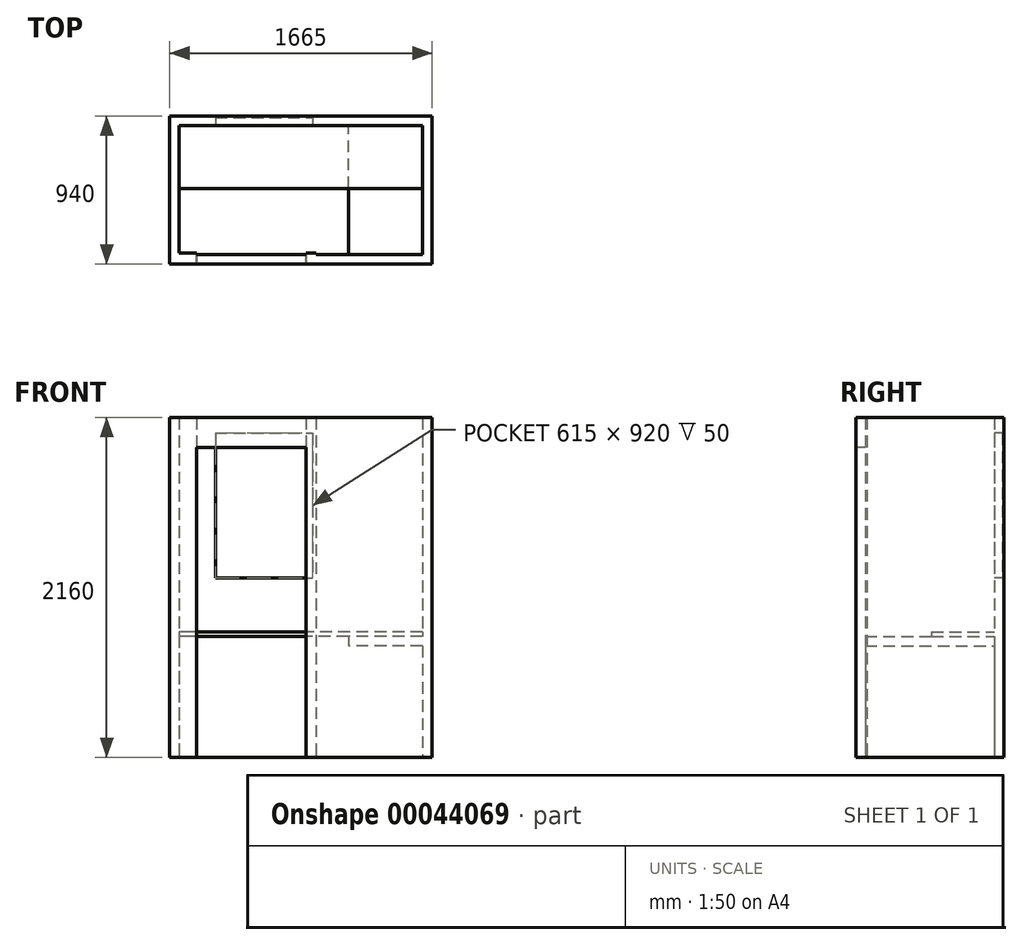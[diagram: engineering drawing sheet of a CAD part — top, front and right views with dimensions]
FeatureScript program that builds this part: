
annotation { "Feature Type Name" : "Feature", "Feature Type Description" : "" }
export const myFeature = defineFeature(function(context is Context, id is Id, definition is map)
    precondition{}
    {
        {
            var Q0;
            Q0=qCreatedBy(makeId("Top.planeOp"),FACE);
            var sketch = newSketch(context, id + "F0", { "sketchPlane" : qUnion([Q0])});
            skLineSegment(sketch, "E0.bottom", {"start": v(-570.89, 899.88) * mm, "end": v(974.11, 899.88) * mm});
            skLineSegment(sketch, "E0.top", {"start": v(234.11, 79.88) * mm, "end": v(974.11, 79.88) * mm});
            skLineSegment(sketch, "E0.left", {"start": v(-570.89, 899.88) * mm, "end": v(-570.89, 79.88) * mm});
            skLineSegment(sketch, "E0.right", {"start": v(974.11, 899.88) * mm, "end": v(974.11, 79.88) * mm});
            skLineSegment(sketch, "E1.0", {"start": v(-630.89, 959.88) * mm, "end": v(1034.11, 959.88) * mm});
            skLineSegment(sketch, "E1.1", {"start": v(-630.89, 959.88) * mm, "end": v(-630.89, 19.88) * mm});
            skLineSegment(sketch, "E1.2", {"start": v(-630.89, 19.88) * mm, "end": v(-570.89, 19.88) * mm});
            skLineSegment(sketch, "E1.3", {"start": v(1034.11, 959.88) * mm, "end": v(1034.11, 19.88) * mm});
            skLineSegment(sketch, "E2", {"start": v(-570.89, 79.88) * mm, "end": v(-570.89, 19.88) * mm});
            skLineSegment(sketch, "E3", {"start": v(234.11, 79.88) * mm, "end": v(234.11, 19.88) * mm});
            skLineSegment(sketch, "E4.trimOffspring", {"start": v(234.11, 19.88) * mm, "end": v(1034.11, 19.88) * mm});
            skLineSegment(sketch, "E5", {"start": v(-570.89, 19.88) * mm, "end": v(-460.89, 19.88) * mm});
            skLineSegment(sketch, "E6", {"start": v(-460.89, 19.88) * mm, "end": v(-460.89, 90.88) * mm});
            skLineSegment(sketch, "E7", {"start": v(-460.89, 90.88) * mm, "end": v(-570.89, 90.88) * mm});
            skLineSegment(sketch, "E8", {"start": v(234.11, 79.88) * mm, "end": v(234.11, 90.88) * mm});
            skLineSegment(sketch, "E9", {"start": v(234.11, 90.88) * mm, "end": v(299.11, 90.88) * mm});
            skLineSegment(sketch, "E10", {"start": v(299.11, 90.88) * mm, "end": v(299.11, 79.88) * mm});
            skSolve(sketch);
        }
        {
            var Q0;
            Q0 = qSketchRegion(id + "F0", true);
            extrude(context, id + "F1", {"entities" : qUnion([Q0]), "depth" : 2160 * mm, "offsetDistance" : 25 * mm});
        }
        {
            var Q0;
            Q0=makeQuery(id+"F1.opExtrude","SWEPT_FACE",FACE,{"disambiguationData":[OSD([sQuery(id+"F0.wireOp",EDGE,"E0.bottom")])]});
            var sketch = newSketch(context, id + "F2", { "sketchPlane" : qUnion([Q0])});
            skLineSegment(sketch, "E11.0", {"start": v(-570.89, 2160) * mm, "end": v(974.11, 2160) * mm});
            skLineSegment(sketch, "E12.0", {"start": v(-570.89, 0) * mm, "end": v(974.11, 0) * mm});
            skLineSegment(sketch, "E13.0", {"start": v(974.11, 2160) * mm, "end": v(974.11, 0) * mm});
            skLineSegment(sketch, "E14.0", {"start": v(-570.89, 2160) * mm, "end": v(-570.89, 0) * mm});
            skPoint(sketch, "E15.bottom.start.orphan", {"position": v(0, 1442.51) * mm});
            skLineSegment(sketch, "E16.bottom", {"start": v(-340.89, 2060) * mm, "end": v(274.11, 2060) * mm});
            skLineSegment(sketch, "E16.top", {"start": v(-340.89, 1140) * mm, "end": v(274.11, 1140) * mm});
            skLineSegment(sketch, "E16.left", {"start": v(-340.89, 2060) * mm, "end": v(-340.89, 1140) * mm});
            skLineSegment(sketch, "E16.right", {"start": v(274.11, 2060) * mm, "end": v(274.11, 1140) * mm});
            skLineSegment(sketch, "E17.bottom", {"start": v(974.11, 769.7) * mm, "end": v(504.11, 769.7) * mm});
            skLineSegment(sketch, "E17.top", {"start": v(974.11, 710) * mm, "end": v(504.11, 710) * mm});
            skLineSegment(sketch, "E17.left", {"start": v(974.11, 769.7) * mm, "end": v(974.11, 710) * mm});
            skLineSegment(sketch, "E17.right", {"start": v(504.11, 769.7) * mm, "end": v(504.11, 710) * mm});
            skLineSegment(sketch, "E18.bottom", {"start": v(974.11, 769.7) * mm, "end": v(-570.89, 769.7) * mm});
            skLineSegment(sketch, "E18.top", {"start": v(974.11, 797.22) * mm, "end": v(-570.89, 797.22) * mm});
            skLineSegment(sketch, "E18.left", {"start": v(974.11, 769.7) * mm, "end": v(974.11, 797.22) * mm});
            skLineSegment(sketch, "E18.right", {"start": v(-570.89, 769.7) * mm, "end": v(-570.89, 797.22) * mm});
            skSolve(sketch);
        }
        {
            var Q0;
            Q0=makeQuery(id+"F2.imprint","IMPRINT",FACE,{"disambiguationData":[TD([[makeQuery(id+"F2.imprint","IMPRINT",EDGE,{"derivedFrom":sQuery(id+"F2.wireOp",EDGE,"E16.bottom")}),-1.0]])]});
            extrude(context, id + "F3", {"entities" : qUnion([Q0]), "operationType" : NewBodyOperationType.REMOVE, "oppositeDirection" : true, "depth" : 50 * mm, "offsetDistance" : 25 * mm});
        }
        {
            var Q0;
            Q0=makeQuery(id+"F2.imprint","IMPRINT",FACE,{"disambiguationData":[TD([[makeQuery(id+"F2.imprint","IMPRINT",EDGE,{"derivedFrom":sQuery(id+"F2.wireOp",EDGE,"E17.bottom")}),1.0]])]});
            var Q1;
            Q1=makeQuery(id+"F2.imprint","IMPRINT",FACE,{"disambiguationData":[TD([[makeQuery(id+"F2.imprint","IMPRINT",EDGE,{"derivedFrom":sQuery(id+"F2.wireOp",EDGE,"E17.top")}),-1.0]])]});
            extrude(context, id + "F4", {"entities" : qUnion([Q0, Q1]), "operationType" : NewBodyOperationType.ADD, "depth" : 850 * mm, "offsetDistance" : 25 * mm});
        }
        {
            var Q0;
            Q0=makeQuery(id+"F1.opExtrude","SWEPT_FACE",FACE,{"disambiguationData":[OSD([sQuery(id+"F0.wireOp",EDGE,"E4.trimOffspring")])]});
            var sketch = newSketch(context, id + "F5", { "sketchPlane" : qUnion([Q0])});
            skLineSegment(sketch, "E19.0", {"start": v(-460.89, 2160) * mm, "end": v(-460.89, 0) * mm});
            skLineSegment(sketch, "E20.0", {"start": v(234.11, 2160) * mm, "end": v(234.11, 0) * mm});
            skLineSegment(sketch, "E21", {"start": v(-460.89, 1970) * mm, "end": v(234.11, 1970) * mm});
            skLineSegment(sketch, "E22", {"start": v(234.11, 2160) * mm, "end": v(-460.89, 2160) * mm});
            skSolve(sketch);
        }
        {
            var Q0;
            Q0 = qSketchRegion(id + "F5", true);
            extrude(context, id + "F6", {"entities" : qUnion([Q0]), "operationType" : NewBodyOperationType.ADD, "oppositeDirection" : true, "depth" : 60 * mm, "offsetDistance" : 25 * mm});
        }
        {
            var Q0;
            Q0=makeQuery(id+"F2.imprint","IMPRINT",FACE,{"disambiguationData":[TD([[makeQuery(id+"F2.imprint","IMPRINT",EDGE,{"derivedFrom":sQuery(id+"F2.wireOp",EDGE,"E18.top")}),1.0]])]});
            extrude(context, id + "F7", {"entities" : qUnion([Q0]), "operationType" : NewBodyOperationType.ADD, "depth" : 400 * mm, "offsetDistance" : 25 * mm});
        }
    });
